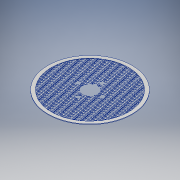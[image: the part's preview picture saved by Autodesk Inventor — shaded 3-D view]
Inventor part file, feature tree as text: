
AUTODESK INVENTOR PART (.ipt)
format: ipt  version: 2018 (Build 220112000, 112)  size: 1,532,928 bytes
history: native  units: mm
features: extrude x5, sketch x4, pattern_linear x2
ambient origin geometry x8: Origin, YZ Plane, XZ Plane, XY Plane, X Axis, Y Axis, Z Axis, Center Point
bodies: Solid1 (feature_tree)
feature tree (11):
  sketch  "Sketch1"  dims[d0=304.8mm d1=279.4mm]
  extrude  "Extrusion1"  Depth=279.4mm
  pattern_linear  "Rectangular Pattern1"  Count1=10 Spacing1=10.5mm
  extrude  "Extrusion4"  Depth=105.0mm
  pattern_linear  "Rectangular Pattern2"  Spacing1=10.0mm  [1 undecoded]
  extrude  "Extrusion2"  Depth=2.0mm TaperAngle=0.0deg
  extrude  "Extrusion3"  TaperAngle=30.0deg  [1 undecoded]
  extrude  "Extrusion5"  Depth=10.5mm
  sketch  "Sketch2"  dims[d2=304.8mm]
  sketch  "Sketch3"  dims[d3=3.0mm d4=100.0mm d6=10.5mm d7=10.0mm d9=10.0mm]
  sketch  "Sketch4"  dims[d11=0.75mm d12=0.0mm d13=30.0mm d15=105.0mm d19=10.0mm d20=0.0mm d21=2.0mm d22=0.0mm d23=30.0deg d24=100.0mm d26=10.5mm d27=10.0mm d29=10.0mm d31=0.75mm d32=0.0mm d33=30.0mm d35=105.0mm d36=55.0mm d37=10.0mm d38=0.0mm d39=40.0mm d41=360.0deg d43=87.3125mm d44=15.875mm]
note: 2 required parameter values undecoded (feature->parameter linkage not recoverable at this tier; creation-order binding heuristic only, values carry confidence <= 0.55)
